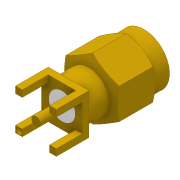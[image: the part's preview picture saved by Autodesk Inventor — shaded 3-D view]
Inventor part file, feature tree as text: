
AUTODESK INVENTOR PART (.ipt)
format: ipt  version: 2017 (Build 210142000, 142)  size: 234,496 bytes
history: native  units: mm
features: sketch x10, extrude x8, revolve x2, fillet x2, projected_geometry x1
ambient origin geometry x8: Origin, YZ Plane, XZ Plane, XY Plane, X Axis, Y Axis, Z Axis, Center Point
bodies: Solid1 (feature_tree)
feature tree (23):
  extrude  "Extrusion1"  Depth=1.0mm
  extrude  "Extrusion2"  Depth=1.0mm
  extrude  "Extrusion3"  Depth=1.0mm
  extrude  "Extrusion4"  Depth=1.0mm
  revolve  "Revolution1"  [1 undecoded]
  revolve  "Revolution2"  [1 undecoded]
  extrude  "Extrusion5"  Depth=3.0mm TaperAngle=0.0deg
  extrude  "Extrusion6"  Depth=8.3mm TaperAngle=0.0deg
  extrude  "Extrusion7"  Depth=2.17mm
  fillet  "Fillet1"  [1 undecoded]
  fillet  "Fillet2"  [1 undecoded]
  extrude  "Extrusion8"  Depth=1.0mm
  sketch  "Sketch1"  dims[d0=1.0mm d1=1.0mm]
  sketch  "Sketch2"  dims[d2=1.0mm d3=1.0mm]
  sketch  "Sketch3"  dims[d4=1.0mm d5=1.0mm]
  sketch  "Sketch4"  dims[d6=1.0mm d7=1.0mm]
  sketch  "Sketch5"  dims[d8=5.1mm d9=5.1mm]
  sketch  "Sketch6"  dims[d10=1.3mm d11=3.9mm d12=0.0mm]
  sketch  "Sketch7"  dims[d13=1.0mm d14=0.0mm d15=3.0mm d16=0.0mm]
  sketch  "Sketch8"  dims[d17=8.0mm d18=8.3mm d19=0.0mm]
  projected_geometry  "Projected Loop1"
  sketch  "Sketch9"  dims[d20=3.825mm d21=2.17mm d22=90.0deg d23=90.0deg]
  sketch  "Sketch10"  dims[d24=6.4mm d25=1.0mm d26=3.0mm d27=0.0mm d28=0.5mm d29=0.0mm d30=5.4mm d31=1.8mm d32=0.0mm d33=0.4mm d34=0.4mm d35=4.0mm d36=0.01mm d37=0.0mm]
note: 4 required parameter values undecoded (feature->parameter linkage not recoverable at this tier; creation-order binding heuristic only, values carry confidence <= 0.55)